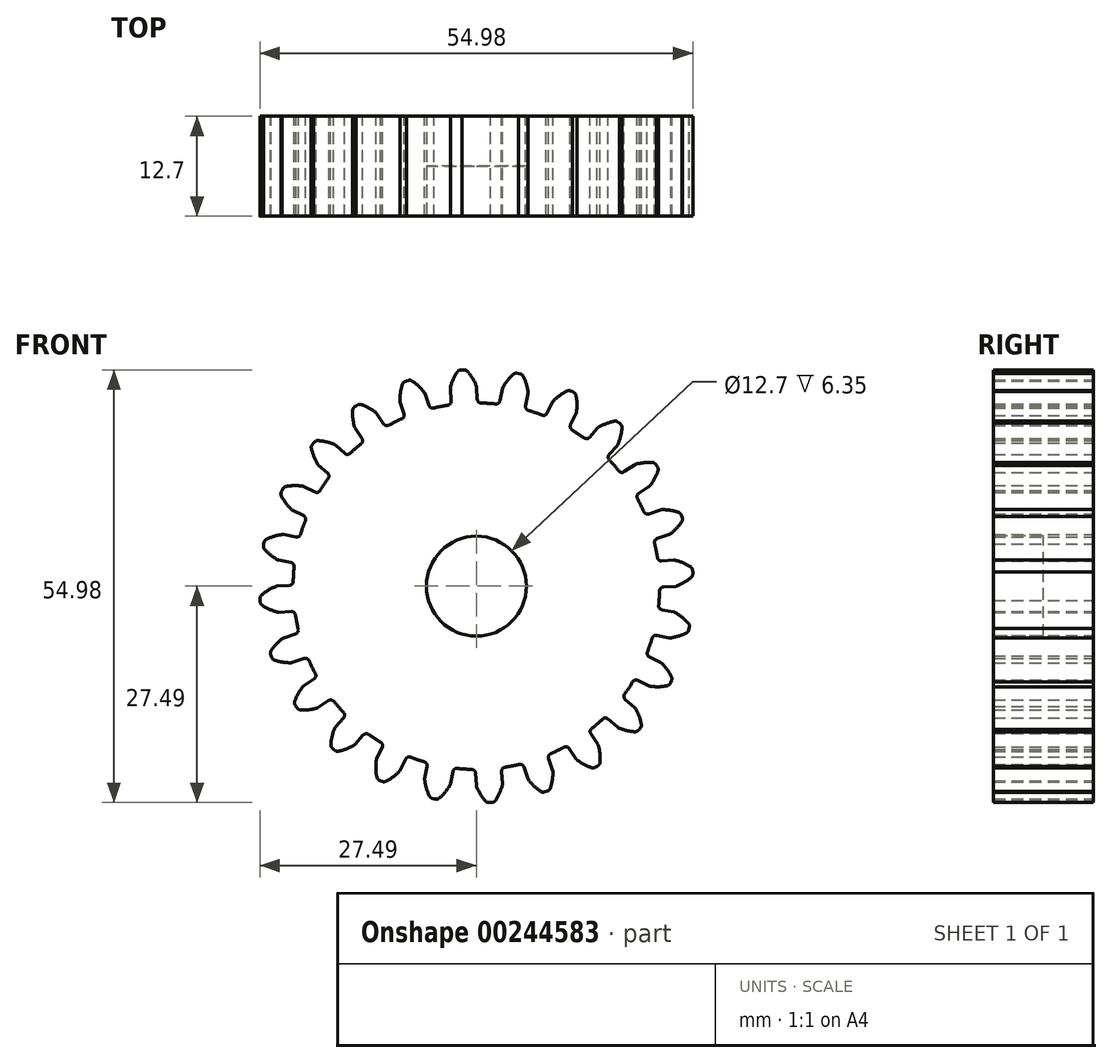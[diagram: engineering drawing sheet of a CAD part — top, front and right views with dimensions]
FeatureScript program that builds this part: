
annotation { "Feature Type Name" : "Feature", "Feature Type Description" : "" }
export const myFeature = defineFeature(function(context is Context, id is Id, definition is map)
    precondition{}
    {
        {
            var Q0;
            Q0=qCreatedBy(makeId("Front.planeOp"),FACE);
            var sketch = newSketch(context, id + "F0", { "sketchPlane" : qUnion([Q0])});
            skArc(sketch, "E0", {"start": v(-3.63, 23) * mm, "mid": v(-4.54, 22.83) * mm, "end": v(-5.44, 22.63) * mm});
            skArc(sketch, "E1", {"start": v(-0.03, 25.48) * mm, "mid": v(-0.52, 26.45) * mm, "end": v(-1.16, 27.32) * mm});
            skLineSegment(sketch, "E2", {"start": v(-1.54, 27.49) * mm, "end": v(-1.8, 27.49) * mm});
            skLineSegment(sketch, "E3", {"start": v(0, 25.32) * mm, "end": v(0.1, 23.75) * mm});
            skLineSegment(sketch, "E4.MirrorCS", {"start": v(-2.06, 27.46) * mm, "end": v(-1.8, 27.49) * mm});
            skArc(sketch, "E5.MirrorCS", {"start": v(-3.3, 25.26) * mm, "mid": v(-2.94, 26.29) * mm, "end": v(-2.41, 27.23) * mm});
            skLineSegment(sketch, "E6.MirrorCS", {"start": v(-3.31, 25.1) * mm, "end": v(-3.2, 23.53) * mm});
            skPoint(sketch, "E7.visualSharp", {"position": v(-3.18, 23.06) * mm});
            skArc(sketch, "E7.filletArc", {"start": v(-3.63, 23) * mm, "mid": v(-3.32, 23.18) * mm, "end": v(-3.2, 23.53) * mm});
            skPoint(sketch, "E8.visualSharp", {"position": v(0.14, 23.28) * mm});
            skArc(sketch, "E8.filletArc", {"start": v(0.1, 23.75) * mm, "mid": v(0.26, 23.41) * mm, "end": v(0.6, 23.27) * mm});
            skPoint(sketch, "E9.visualSharp", {"position": v(0, 25.4) * mm});
            skArc(sketch, "E9.filletArc", {"start": v(0, 25.32) * mm, "mid": v(0, 25.4) * mm, "end": v(-0.03, 25.48) * mm});
            skPoint(sketch, "E10.visualSharp", {"position": v(-1.32, 27.49) * mm});
            skArc(sketch, "E10.filletArc", {"start": v(-1.16, 27.32) * mm, "mid": v(-1.33, 27.44) * mm, "end": v(-1.54, 27.49) * mm});
            skPoint(sketch, "E11.visualSharp", {"position": v(-2.28, 27.43) * mm});
            skArc(sketch, "E11.filletArc", {"start": v(-2.06, 27.46) * mm, "mid": v(-2.26, 27.38) * mm, "end": v(-2.41, 27.23) * mm});
            skPoint(sketch, "E12.visualSharp", {"position": v(-3.32, 25.18) * mm});
            skArc(sketch, "E12.filletArc", {"start": v(-3.3, 25.26) * mm, "mid": v(-3.3, 25.18) * mm, "end": v(-3.31, 25.1) * mm});
            skArc(sketch, "E13.1.0", {"start": v(-9.46, 21.27) * mm, "mid": v(-9.2, 21.53) * mm, "end": v(-9.19, 21.9) * mm});
            skLineSegment(sketch, "E13.1.1", {"start": v(-9.7, 23.4) * mm, "end": v(-9.19, 21.9) * mm});
            skArc(sketch, "E13.1.2", {"start": v(-6.04, 22.96) * mm, "mid": v(-5.8, 22.68) * mm, "end": v(-5.44, 22.63) * mm});
            skLineSegment(sketch, "E13.1.3", {"start": v(-6.55, 24.46) * mm, "end": v(-6.04, 22.96) * mm});
            skArc(sketch, "E13.1.4", {"start": v(-6.62, 24.6) * mm, "mid": v(-7.34, 25.41) * mm, "end": v(-8.2, 26.09) * mm});
            skArc(sketch, "E13.1.5", {"start": v(-9.72, 23.55) * mm, "mid": v(-9.64, 24.63) * mm, "end": v(-9.38, 25.68) * mm});
            skArc(sketch, "E13.1.6", {"start": v(-9.1, 25.99) * mm, "mid": v(-9.27, 25.87) * mm, "end": v(-9.38, 25.68) * mm});
            skLineSegment(sketch, "E13.1.7", {"start": v(-8.6, 26.15) * mm, "end": v(-8.86, 26.09) * mm});
            skLineSegment(sketch, "E13.1.8", {"start": v(-9.1, 25.99) * mm, "end": v(-8.86, 26.09) * mm});
            skArc(sketch, "E13.1.9", {"start": v(-8.2, 26.09) * mm, "mid": v(-8.4, 26.16) * mm, "end": v(-8.6, 26.15) * mm});
            skArc(sketch, "E13.1.10", {"start": v(-6.55, 24.46) * mm, "mid": v(-6.58, 24.53) * mm, "end": v(-6.62, 24.6) * mm});
            skArc(sketch, "E13.1.11", {"start": v(-9.72, 23.55) * mm, "mid": v(-9.71, 23.47) * mm, "end": v(-9.7, 23.4) * mm});
            skArc(sketch, "E13.2.0", {"start": v(-14.64, 18.1) * mm, "mid": v(-14.46, 18.41) * mm, "end": v(-14.54, 18.77) * mm});
            skLineSegment(sketch, "E13.2.1", {"start": v(-15.42, 20.09) * mm, "end": v(-14.54, 18.77) * mm});
            skArc(sketch, "E13.2.2", {"start": v(-11.78, 20.62) * mm, "mid": v(-11.48, 20.4) * mm, "end": v(-11.11, 20.45) * mm});
            skLineSegment(sketch, "E13.2.3", {"start": v(-12.66, 21.93) * mm, "end": v(-11.78, 20.62) * mm});
            skArc(sketch, "E13.2.4", {"start": v(-12.76, 22.05) * mm, "mid": v(-13.67, 22.64) * mm, "end": v(-14.66, 23.08) * mm});
            skArc(sketch, "E13.2.5", {"start": v(-15.49, 20.23) * mm, "mid": v(-15.69, 21.3) * mm, "end": v(-15.7, 22.38) * mm});
            skArc(sketch, "E13.2.6", {"start": v(-15.51, 22.75) * mm, "mid": v(-15.65, 22.58) * mm, "end": v(-15.7, 22.38) * mm});
            skLineSegment(sketch, "E13.2.7", {"start": v(-15.08, 23.04) * mm, "end": v(-15.3, 22.9) * mm});
            skLineSegment(sketch, "E13.2.8", {"start": v(-15.51, 22.75) * mm, "end": v(-15.3, 22.9) * mm});
            skArc(sketch, "E13.2.9", {"start": v(-14.66, 23.08) * mm, "mid": v(-14.88, 23.1) * mm, "end": v(-15.08, 23.04) * mm});
            skArc(sketch, "E13.2.10", {"start": v(-12.66, 21.93) * mm, "mid": v(-12.7, 22) * mm, "end": v(-12.76, 22.05) * mm});
            skArc(sketch, "E13.2.11", {"start": v(-15.49, 20.23) * mm, "mid": v(-15.46, 20.16) * mm, "end": v(-15.42, 20.09) * mm});
            skArc(sketch, "E13.3.0", {"start": v(-18.83, 13.69) * mm, "mid": v(-18.73, 14.04) * mm, "end": v(-18.9, 14.37) * mm});
            skLineSegment(sketch, "E13.3.1", {"start": v(-20.1, 15.41) * mm, "end": v(-18.9, 14.37) * mm});
            skArc(sketch, "E13.3.2", {"start": v(-16.71, 16.87) * mm, "mid": v(-16.37, 16.74) * mm, "end": v(-16.03, 16.88) * mm});
            skLineSegment(sketch, "E13.3.3", {"start": v(-17.9, 17.9) * mm, "end": v(-16.71, 16.87) * mm});
            skArc(sketch, "E13.3.4", {"start": v(-18.04, 18) * mm, "mid": v(-19.06, 18.33) * mm, "end": v(-20.14, 18.5) * mm});
            skArc(sketch, "E13.3.5", {"start": v(-20.2, 15.53) * mm, "mid": v(-20.67, 16.5) * mm, "end": v(-20.97, 17.55) * mm});
            skArc(sketch, "E13.3.6", {"start": v(-20.87, 17.96) * mm, "mid": v(-20.96, 17.76) * mm, "end": v(-20.97, 17.55) * mm});
            skLineSegment(sketch, "E13.3.7", {"start": v(-20.53, 18.35) * mm, "end": v(-20.71, 18.16) * mm});
            skLineSegment(sketch, "E13.3.8", {"start": v(-20.87, 17.96) * mm, "end": v(-20.71, 18.16) * mm});
            skArc(sketch, "E13.3.9", {"start": v(-20.14, 18.5) * mm, "mid": v(-20.35, 18.46) * mm, "end": v(-20.53, 18.35) * mm});
            skArc(sketch, "E13.3.10", {"start": v(-17.9, 17.9) * mm, "mid": v(-17.97, 17.96) * mm, "end": v(-18.04, 18) * mm});
            skArc(sketch, "E13.3.11", {"start": v(-20.2, 15.53) * mm, "mid": v(-20.15, 15.47) * mm, "end": v(-20.1, 15.41) * mm});
            skArc(sketch, "E13.4.0", {"start": v(-21.73, 8.35) * mm, "mid": v(-21.73, 8.72) * mm, "end": v(-21.98, 8.99) * mm});
            skLineSegment(sketch, "E13.4.1", {"start": v(-23.4, 9.69) * mm, "end": v(-21.98, 8.99) * mm});
            skArc(sketch, "E13.4.2", {"start": v(-20.51, 11.97) * mm, "mid": v(-20.14, 11.93) * mm, "end": v(-19.85, 12.16) * mm});
            skLineSegment(sketch, "E13.4.3", {"start": v(-21.93, 12.67) * mm, "end": v(-20.51, 11.97) * mm});
            skArc(sketch, "E13.4.4", {"start": v(-22.08, 12.71) * mm, "mid": v(-23.16, 12.78) * mm, "end": v(-24.24, 12.65) * mm});
            skArc(sketch, "E13.4.5", {"start": v(-23.53, 9.78) * mm, "mid": v(-24.23, 10.6) * mm, "end": v(-24.8, 11.53) * mm});
            skArc(sketch, "E13.4.6", {"start": v(-24.8, 11.94) * mm, "mid": v(-24.85, 11.73) * mm, "end": v(-24.8, 11.53) * mm});
            skLineSegment(sketch, "E13.4.7", {"start": v(-24.58, 12.4) * mm, "end": v(-24.7, 12.18) * mm});
            skLineSegment(sketch, "E13.4.8", {"start": v(-24.8, 11.94) * mm, "end": v(-24.7, 12.18) * mm});
            skArc(sketch, "E13.4.9", {"start": v(-24.24, 12.65) * mm, "mid": v(-24.43, 12.57) * mm, "end": v(-24.58, 12.4) * mm});
            skArc(sketch, "E13.4.10", {"start": v(-21.93, 12.67) * mm, "mid": v(-22, 12.7) * mm, "end": v(-22.08, 12.71) * mm});
            skArc(sketch, "E13.4.11", {"start": v(-23.53, 9.78) * mm, "mid": v(-23.46, 9.73) * mm, "end": v(-23.4, 9.69) * mm});
            skArc(sketch, "E13.5.0", {"start": v(-23.15, 2.44) * mm, "mid": v(-23.25, 2.8) * mm, "end": v(-23.56, 3) * mm});
            skLineSegment(sketch, "E13.5.1", {"start": v(-25.1, 3.3) * mm, "end": v(-23.56, 3) * mm});
            skArc(sketch, "E13.5.2", {"start": v(-22.9, 6.25) * mm, "mid": v(-22.55, 6.31) * mm, "end": v(-22.32, 6.6) * mm});
            skLineSegment(sketch, "E13.5.3", {"start": v(-24.46, 6.56) * mm, "end": v(-22.9, 6.25) * mm});
            skArc(sketch, "E13.5.4", {"start": v(-24.62, 6.56) * mm, "mid": v(-25.68, 6.35) * mm, "end": v(-26.69, 5.95) * mm});
            skArc(sketch, "E13.5.5", {"start": v(-25.25, 3.36) * mm, "mid": v(-26.15, 3.96) * mm, "end": v(-26.93, 4.72) * mm});
            skArc(sketch, "E13.5.6", {"start": v(-27.05, 5.12) * mm, "mid": v(-27.04, 4.9) * mm, "end": v(-26.93, 4.72) * mm});
            skLineSegment(sketch, "E13.5.7", {"start": v(-26.95, 5.63) * mm, "end": v(-27.02, 5.37) * mm});
            skLineSegment(sketch, "E13.5.8", {"start": v(-27.05, 5.12) * mm, "end": v(-27.02, 5.37) * mm});
            skArc(sketch, "E13.5.9", {"start": v(-26.69, 5.95) * mm, "mid": v(-26.85, 5.82) * mm, "end": v(-26.95, 5.63) * mm});
            skArc(sketch, "E13.5.10", {"start": v(-24.46, 6.56) * mm, "mid": v(-24.54, 6.57) * mm, "end": v(-24.62, 6.56) * mm});
            skArc(sketch, "E13.5.11", {"start": v(-25.25, 3.36) * mm, "mid": v(-25.18, 3.32) * mm, "end": v(-25.1, 3.3) * mm});
            skArc(sketch, "E13.6.0", {"start": v(-23, -3.63) * mm, "mid": v(-23.18, -3.32) * mm, "end": v(-23.53, -3.2) * mm});
            skLineSegment(sketch, "E13.6.1", {"start": v(-25.1, -3.31) * mm, "end": v(-23.53, -3.2) * mm});
            skArc(sketch, "E13.6.2", {"start": v(-23.75, 0.1) * mm, "mid": v(-23.41, 0.26) * mm, "end": v(-23.27, 0.6) * mm});
            skLineSegment(sketch, "E13.6.3", {"start": v(-25.32, 0) * mm, "end": v(-23.75, 0.1) * mm});
            skArc(sketch, "E13.6.4", {"start": v(-25.48, -0.03) * mm, "mid": v(-26.45, -0.52) * mm, "end": v(-27.32, -1.16) * mm});
            skArc(sketch, "E13.6.5", {"start": v(-25.26, -3.3) * mm, "mid": v(-26.29, -2.94) * mm, "end": v(-27.23, -2.41) * mm});
            skArc(sketch, "E13.6.6", {"start": v(-27.46, -2.06) * mm, "mid": v(-27.38, -2.26) * mm, "end": v(-27.23, -2.41) * mm});
            skLineSegment(sketch, "E13.6.7", {"start": v(-27.49, -1.54) * mm, "end": v(-27.49, -1.8) * mm});
            skLineSegment(sketch, "E13.6.8", {"start": v(-27.46, -2.06) * mm, "end": v(-27.49, -1.8) * mm});
            skArc(sketch, "E13.6.9", {"start": v(-27.32, -1.16) * mm, "mid": v(-27.44, -1.33) * mm, "end": v(-27.49, -1.54) * mm});
            skArc(sketch, "E13.6.10", {"start": v(-25.32, 0) * mm, "mid": v(-25.4, 0) * mm, "end": v(-25.48, -0.03) * mm});
            skArc(sketch, "E13.6.11", {"start": v(-25.26, -3.3) * mm, "mid": v(-25.18, -3.3) * mm, "end": v(-25.1, -3.31) * mm});
            skArc(sketch, "E13.7.0", {"start": v(-21.27, -9.46) * mm, "mid": v(-21.53, -9.2) * mm, "end": v(-21.9, -9.19) * mm});
            skLineSegment(sketch, "E13.7.1", {"start": v(-23.4, -9.7) * mm, "end": v(-21.9, -9.19) * mm});
            skArc(sketch, "E13.7.2", {"start": v(-22.96, -6.04) * mm, "mid": v(-22.68, -5.8) * mm, "end": v(-22.63, -5.44) * mm});
            skLineSegment(sketch, "E13.7.3", {"start": v(-24.46, -6.55) * mm, "end": v(-22.96, -6.04) * mm});
            skArc(sketch, "E13.7.4", {"start": v(-24.6, -6.62) * mm, "mid": v(-25.41, -7.34) * mm, "end": v(-26.09, -8.2) * mm});
            skArc(sketch, "E13.7.5", {"start": v(-23.55, -9.72) * mm, "mid": v(-24.63, -9.64) * mm, "end": v(-25.68, -9.38) * mm});
            skArc(sketch, "E13.7.6", {"start": v(-25.99, -9.1) * mm, "mid": v(-25.87, -9.27) * mm, "end": v(-25.68, -9.38) * mm});
            skLineSegment(sketch, "E13.7.7", {"start": v(-26.15, -8.6) * mm, "end": v(-26.09, -8.86) * mm});
            skLineSegment(sketch, "E13.7.8", {"start": v(-25.99, -9.1) * mm, "end": v(-26.09, -8.86) * mm});
            skArc(sketch, "E13.7.9", {"start": v(-26.09, -8.2) * mm, "mid": v(-26.16, -8.4) * mm, "end": v(-26.15, -8.6) * mm});
            skArc(sketch, "E13.7.10", {"start": v(-24.46, -6.55) * mm, "mid": v(-24.53, -6.58) * mm, "end": v(-24.6, -6.62) * mm});
            skArc(sketch, "E13.7.11", {"start": v(-23.55, -9.72) * mm, "mid": v(-23.47, -9.71) * mm, "end": v(-23.4, -9.7) * mm});
            skArc(sketch, "E13.8.0", {"start": v(-18.1, -14.64) * mm, "mid": v(-18.41, -14.46) * mm, "end": v(-18.77, -14.54) * mm});
            skLineSegment(sketch, "E13.8.1", {"start": v(-20.09, -15.42) * mm, "end": v(-18.77, -14.54) * mm});
            skArc(sketch, "E13.8.2", {"start": v(-20.62, -11.78) * mm, "mid": v(-20.4, -11.48) * mm, "end": v(-20.45, -11.11) * mm});
            skLineSegment(sketch, "E13.8.3", {"start": v(-21.93, -12.66) * mm, "end": v(-20.62, -11.78) * mm});
            skArc(sketch, "E13.8.4", {"start": v(-22.05, -12.76) * mm, "mid": v(-22.64, -13.67) * mm, "end": v(-23.08, -14.66) * mm});
            skArc(sketch, "E13.8.5", {"start": v(-20.23, -15.49) * mm, "mid": v(-21.3, -15.69) * mm, "end": v(-22.38, -15.7) * mm});
            skArc(sketch, "E13.8.6", {"start": v(-22.75, -15.51) * mm, "mid": v(-22.58, -15.65) * mm, "end": v(-22.38, -15.7) * mm});
            skLineSegment(sketch, "E13.8.7", {"start": v(-23.04, -15.08) * mm, "end": v(-22.9, -15.3) * mm});
            skLineSegment(sketch, "E13.8.8", {"start": v(-22.75, -15.51) * mm, "end": v(-22.9, -15.3) * mm});
            skArc(sketch, "E13.8.9", {"start": v(-23.08, -14.66) * mm, "mid": v(-23.1, -14.88) * mm, "end": v(-23.04, -15.08) * mm});
            skArc(sketch, "E13.8.10", {"start": v(-21.93, -12.66) * mm, "mid": v(-22, -12.7) * mm, "end": v(-22.05, -12.76) * mm});
            skArc(sketch, "E13.8.11", {"start": v(-20.23, -15.49) * mm, "mid": v(-20.16, -15.46) * mm, "end": v(-20.09, -15.42) * mm});
            skArc(sketch, "E13.9.0", {"start": v(-13.69, -18.83) * mm, "mid": v(-14.04, -18.73) * mm, "end": v(-14.37, -18.9) * mm});
            skLineSegment(sketch, "E13.9.1", {"start": v(-15.41, -20.1) * mm, "end": v(-14.37, -18.9) * mm});
            skArc(sketch, "E13.9.2", {"start": v(-16.87, -16.71) * mm, "mid": v(-16.74, -16.37) * mm, "end": v(-16.88, -16.03) * mm});
            skLineSegment(sketch, "E13.9.3", {"start": v(-17.9, -17.9) * mm, "end": v(-16.87, -16.71) * mm});
            skArc(sketch, "E13.9.4", {"start": v(-18, -18.04) * mm, "mid": v(-18.33, -19.06) * mm, "end": v(-18.5, -20.14) * mm});
            skArc(sketch, "E13.9.5", {"start": v(-15.53, -20.2) * mm, "mid": v(-16.5, -20.67) * mm, "end": v(-17.55, -20.97) * mm});
            skArc(sketch, "E13.9.6", {"start": v(-17.96, -20.87) * mm, "mid": v(-17.76, -20.96) * mm, "end": v(-17.55, -20.97) * mm});
            skLineSegment(sketch, "E13.9.7", {"start": v(-18.35, -20.53) * mm, "end": v(-18.16, -20.71) * mm});
            skLineSegment(sketch, "E13.9.8", {"start": v(-17.96, -20.87) * mm, "end": v(-18.16, -20.71) * mm});
            skArc(sketch, "E13.9.9", {"start": v(-18.5, -20.14) * mm, "mid": v(-18.46, -20.35) * mm, "end": v(-18.35, -20.53) * mm});
            skArc(sketch, "E13.9.10", {"start": v(-17.9, -17.9) * mm, "mid": v(-17.96, -17.97) * mm, "end": v(-18, -18.04) * mm});
            skArc(sketch, "E13.9.11", {"start": v(-15.53, -20.2) * mm, "mid": v(-15.47, -20.15) * mm, "end": v(-15.41, -20.1) * mm});
            skArc(sketch, "E13.10.0", {"start": v(-8.35, -21.73) * mm, "mid": v(-8.72, -21.73) * mm, "end": v(-8.99, -21.98) * mm});
            skLineSegment(sketch, "E13.10.1", {"start": v(-9.69, -23.4) * mm, "end": v(-8.99, -21.98) * mm});
            skArc(sketch, "E13.10.2", {"start": v(-11.97, -20.51) * mm, "mid": v(-11.93, -20.14) * mm, "end": v(-12.16, -19.85) * mm});
            skLineSegment(sketch, "E13.10.3", {"start": v(-12.67, -21.93) * mm, "end": v(-11.97, -20.51) * mm});
            skArc(sketch, "E13.10.4", {"start": v(-12.71, -22.08) * mm, "mid": v(-12.78, -23.16) * mm, "end": v(-12.65, -24.24) * mm});
            skArc(sketch, "E13.10.5", {"start": v(-9.78, -23.53) * mm, "mid": v(-10.6, -24.23) * mm, "end": v(-11.53, -24.8) * mm});
            skArc(sketch, "E13.10.6", {"start": v(-11.94, -24.8) * mm, "mid": v(-11.73, -24.85) * mm, "end": v(-11.53, -24.8) * mm});
            skLineSegment(sketch, "E13.10.7", {"start": v(-12.4, -24.58) * mm, "end": v(-12.18, -24.7) * mm});
            skLineSegment(sketch, "E13.10.8", {"start": v(-11.94, -24.8) * mm, "end": v(-12.18, -24.7) * mm});
            skArc(sketch, "E13.10.9", {"start": v(-12.65, -24.24) * mm, "mid": v(-12.57, -24.43) * mm, "end": v(-12.4, -24.58) * mm});
            skArc(sketch, "E13.10.10", {"start": v(-12.67, -21.93) * mm, "mid": v(-12.7, -22) * mm, "end": v(-12.71, -22.08) * mm});
            skArc(sketch, "E13.10.11", {"start": v(-9.78, -23.53) * mm, "mid": v(-9.73, -23.46) * mm, "end": v(-9.69, -23.4) * mm});
            skArc(sketch, "E13.11.0", {"start": v(-2.44, -23.15) * mm, "mid": v(-2.8, -23.25) * mm, "end": v(-3, -23.56) * mm});
            skLineSegment(sketch, "E13.11.1", {"start": v(-3.3, -25.1) * mm, "end": v(-3, -23.56) * mm});
            skArc(sketch, "E13.11.2", {"start": v(-6.25, -22.9) * mm, "mid": v(-6.31, -22.55) * mm, "end": v(-6.6, -22.32) * mm});
            skLineSegment(sketch, "E13.11.3", {"start": v(-6.56, -24.46) * mm, "end": v(-6.25, -22.9) * mm});
            skArc(sketch, "E13.11.4", {"start": v(-6.56, -24.62) * mm, "mid": v(-6.35, -25.68) * mm, "end": v(-5.95, -26.69) * mm});
            skArc(sketch, "E13.11.5", {"start": v(-3.36, -25.25) * mm, "mid": v(-3.96, -26.15) * mm, "end": v(-4.72, -26.93) * mm});
            skArc(sketch, "E13.11.6", {"start": v(-5.12, -27.05) * mm, "mid": v(-4.9, -27.04) * mm, "end": v(-4.72, -26.93) * mm});
            skLineSegment(sketch, "E13.11.7", {"start": v(-5.63, -26.95) * mm, "end": v(-5.37, -27.02) * mm});
            skLineSegment(sketch, "E13.11.8", {"start": v(-5.12, -27.05) * mm, "end": v(-5.37, -27.02) * mm});
            skArc(sketch, "E13.11.9", {"start": v(-5.95, -26.69) * mm, "mid": v(-5.82, -26.85) * mm, "end": v(-5.63, -26.95) * mm});
            skArc(sketch, "E13.11.10", {"start": v(-6.56, -24.46) * mm, "mid": v(-6.57, -24.54) * mm, "end": v(-6.56, -24.62) * mm});
            skArc(sketch, "E13.11.11", {"start": v(-3.36, -25.25) * mm, "mid": v(-3.32, -25.18) * mm, "end": v(-3.3, -25.1) * mm});
            skArc(sketch, "E13.12.0", {"start": v(3.63, -23) * mm, "mid": v(3.32, -23.18) * mm, "end": v(3.2, -23.53) * mm});
            skLineSegment(sketch, "E13.12.1", {"start": v(3.31, -25.1) * mm, "end": v(3.2, -23.53) * mm});
            skArc(sketch, "E13.12.2", {"start": v(-0.1, -23.75) * mm, "mid": v(-0.26, -23.41) * mm, "end": v(-0.6, -23.27) * mm});
            skLineSegment(sketch, "E13.12.3", {"start": v(0, -25.32) * mm, "end": v(-0.1, -23.75) * mm});
            skArc(sketch, "E13.12.4", {"start": v(0.03, -25.48) * mm, "mid": v(0.52, -26.45) * mm, "end": v(1.16, -27.32) * mm});
            skArc(sketch, "E13.12.5", {"start": v(3.3, -25.26) * mm, "mid": v(2.94, -26.29) * mm, "end": v(2.41, -27.23) * mm});
            skArc(sketch, "E13.12.6", {"start": v(2.06, -27.46) * mm, "mid": v(2.26, -27.38) * mm, "end": v(2.41, -27.23) * mm});
            skLineSegment(sketch, "E13.12.7", {"start": v(1.54, -27.49) * mm, "end": v(1.8, -27.49) * mm});
            skLineSegment(sketch, "E13.12.8", {"start": v(2.06, -27.46) * mm, "end": v(1.8, -27.49) * mm});
            skArc(sketch, "E13.12.9", {"start": v(1.16, -27.32) * mm, "mid": v(1.33, -27.44) * mm, "end": v(1.54, -27.49) * mm});
            skArc(sketch, "E13.12.10", {"start": v(0, -25.32) * mm, "mid": v(0, -25.4) * mm, "end": v(0.03, -25.48) * mm});
            skArc(sketch, "E13.12.11", {"start": v(3.3, -25.26) * mm, "mid": v(3.3, -25.18) * mm, "end": v(3.31, -25.1) * mm});
            skArc(sketch, "E13.13.0", {"start": v(9.46, -21.27) * mm, "mid": v(9.2, -21.53) * mm, "end": v(9.19, -21.9) * mm});
            skLineSegment(sketch, "E13.13.1", {"start": v(9.7, -23.4) * mm, "end": v(9.19, -21.9) * mm});
            skArc(sketch, "E13.13.2", {"start": v(6.04, -22.96) * mm, "mid": v(5.8, -22.68) * mm, "end": v(5.44, -22.63) * mm});
            skLineSegment(sketch, "E13.13.3", {"start": v(6.55, -24.46) * mm, "end": v(6.04, -22.96) * mm});
            skArc(sketch, "E13.13.4", {"start": v(6.62, -24.6) * mm, "mid": v(7.34, -25.41) * mm, "end": v(8.2, -26.09) * mm});
            skArc(sketch, "E13.13.5", {"start": v(9.72, -23.55) * mm, "mid": v(9.64, -24.63) * mm, "end": v(9.38, -25.68) * mm});
            skArc(sketch, "E13.13.6", {"start": v(9.1, -25.99) * mm, "mid": v(9.27, -25.87) * mm, "end": v(9.38, -25.68) * mm});
            skLineSegment(sketch, "E13.13.7", {"start": v(8.6, -26.15) * mm, "end": v(8.86, -26.09) * mm});
            skLineSegment(sketch, "E13.13.8", {"start": v(9.1, -25.99) * mm, "end": v(8.86, -26.09) * mm});
            skArc(sketch, "E13.13.9", {"start": v(8.2, -26.09) * mm, "mid": v(8.4, -26.16) * mm, "end": v(8.6, -26.15) * mm});
            skArc(sketch, "E13.13.10", {"start": v(6.55, -24.46) * mm, "mid": v(6.58, -24.53) * mm, "end": v(6.62, -24.6) * mm});
            skArc(sketch, "E13.13.11", {"start": v(9.72, -23.55) * mm, "mid": v(9.71, -23.47) * mm, "end": v(9.7, -23.4) * mm});
            skArc(sketch, "E13.14.0", {"start": v(14.64, -18.1) * mm, "mid": v(14.46, -18.41) * mm, "end": v(14.54, -18.77) * mm});
            skLineSegment(sketch, "E13.14.1", {"start": v(15.42, -20.09) * mm, "end": v(14.54, -18.77) * mm});
            skArc(sketch, "E13.14.2", {"start": v(11.78, -20.62) * mm, "mid": v(11.48, -20.4) * mm, "end": v(11.11, -20.45) * mm});
            skLineSegment(sketch, "E13.14.3", {"start": v(12.66, -21.93) * mm, "end": v(11.78, -20.62) * mm});
            skArc(sketch, "E13.14.4", {"start": v(12.76, -22.05) * mm, "mid": v(13.67, -22.64) * mm, "end": v(14.66, -23.08) * mm});
            skArc(sketch, "E13.14.5", {"start": v(15.49, -20.23) * mm, "mid": v(15.69, -21.3) * mm, "end": v(15.7, -22.38) * mm});
            skArc(sketch, "E13.14.6", {"start": v(15.51, -22.75) * mm, "mid": v(15.65, -22.58) * mm, "end": v(15.7, -22.38) * mm});
            skLineSegment(sketch, "E13.14.7", {"start": v(15.08, -23.04) * mm, "end": v(15.3, -22.9) * mm});
            skLineSegment(sketch, "E13.14.8", {"start": v(15.51, -22.75) * mm, "end": v(15.3, -22.9) * mm});
            skArc(sketch, "E13.14.9", {"start": v(14.66, -23.08) * mm, "mid": v(14.88, -23.1) * mm, "end": v(15.08, -23.04) * mm});
            skArc(sketch, "E13.14.10", {"start": v(12.66, -21.93) * mm, "mid": v(12.7, -22) * mm, "end": v(12.76, -22.05) * mm});
            skArc(sketch, "E13.14.11", {"start": v(15.49, -20.23) * mm, "mid": v(15.46, -20.16) * mm, "end": v(15.42, -20.09) * mm});
            skArc(sketch, "E13.15.0", {"start": v(18.83, -13.69) * mm, "mid": v(18.73, -14.04) * mm, "end": v(18.9, -14.37) * mm});
            skLineSegment(sketch, "E13.15.1", {"start": v(20.1, -15.41) * mm, "end": v(18.9, -14.37) * mm});
            skArc(sketch, "E13.15.2", {"start": v(16.71, -16.87) * mm, "mid": v(16.37, -16.74) * mm, "end": v(16.03, -16.88) * mm});
            skLineSegment(sketch, "E13.15.3", {"start": v(17.9, -17.9) * mm, "end": v(16.71, -16.87) * mm});
            skArc(sketch, "E13.15.4", {"start": v(18.04, -18) * mm, "mid": v(19.06, -18.33) * mm, "end": v(20.14, -18.5) * mm});
            skArc(sketch, "E13.15.5", {"start": v(20.2, -15.53) * mm, "mid": v(20.67, -16.5) * mm, "end": v(20.97, -17.55) * mm});
            skArc(sketch, "E13.15.6", {"start": v(20.87, -17.96) * mm, "mid": v(20.96, -17.76) * mm, "end": v(20.97, -17.55) * mm});
            skLineSegment(sketch, "E13.15.7", {"start": v(20.53, -18.35) * mm, "end": v(20.71, -18.16) * mm});
            skLineSegment(sketch, "E13.15.8", {"start": v(20.87, -17.96) * mm, "end": v(20.71, -18.16) * mm});
            skArc(sketch, "E13.15.9", {"start": v(20.14, -18.5) * mm, "mid": v(20.35, -18.46) * mm, "end": v(20.53, -18.35) * mm});
            skArc(sketch, "E13.15.10", {"start": v(17.9, -17.9) * mm, "mid": v(17.97, -17.96) * mm, "end": v(18.04, -18) * mm});
            skArc(sketch, "E13.15.11", {"start": v(20.2, -15.53) * mm, "mid": v(20.15, -15.47) * mm, "end": v(20.1, -15.41) * mm});
            skArc(sketch, "E13.16.0", {"start": v(21.73, -8.35) * mm, "mid": v(21.73, -8.72) * mm, "end": v(21.98, -8.99) * mm});
            skLineSegment(sketch, "E13.16.1", {"start": v(23.4, -9.69) * mm, "end": v(21.98, -8.99) * mm});
            skArc(sketch, "E13.16.2", {"start": v(20.51, -11.97) * mm, "mid": v(20.14, -11.93) * mm, "end": v(19.85, -12.16) * mm});
            skLineSegment(sketch, "E13.16.3", {"start": v(21.93, -12.67) * mm, "end": v(20.51, -11.97) * mm});
            skArc(sketch, "E13.16.4", {"start": v(22.08, -12.71) * mm, "mid": v(23.16, -12.78) * mm, "end": v(24.24, -12.65) * mm});
            skArc(sketch, "E13.16.5", {"start": v(23.53, -9.78) * mm, "mid": v(24.23, -10.6) * mm, "end": v(24.8, -11.53) * mm});
            skArc(sketch, "E13.16.6", {"start": v(24.8, -11.94) * mm, "mid": v(24.85, -11.73) * mm, "end": v(24.8, -11.53) * mm});
            skLineSegment(sketch, "E13.16.7", {"start": v(24.58, -12.4) * mm, "end": v(24.7, -12.18) * mm});
            skLineSegment(sketch, "E13.16.8", {"start": v(24.8, -11.94) * mm, "end": v(24.7, -12.18) * mm});
            skArc(sketch, "E13.16.9", {"start": v(24.24, -12.65) * mm, "mid": v(24.43, -12.57) * mm, "end": v(24.58, -12.4) * mm});
            skArc(sketch, "E13.16.10", {"start": v(21.93, -12.67) * mm, "mid": v(22, -12.7) * mm, "end": v(22.08, -12.71) * mm});
            skArc(sketch, "E13.16.11", {"start": v(23.53, -9.78) * mm, "mid": v(23.46, -9.73) * mm, "end": v(23.4, -9.69) * mm});
            skArc(sketch, "E13.17.0", {"start": v(23.15, -2.44) * mm, "mid": v(23.25, -2.8) * mm, "end": v(23.56, -3) * mm});
            skLineSegment(sketch, "E13.17.1", {"start": v(25.1, -3.3) * mm, "end": v(23.56, -3) * mm});
            skArc(sketch, "E13.17.2", {"start": v(22.9, -6.25) * mm, "mid": v(22.55, -6.31) * mm, "end": v(22.32, -6.6) * mm});
            skLineSegment(sketch, "E13.17.3", {"start": v(24.46, -6.56) * mm, "end": v(22.9, -6.25) * mm});
            skArc(sketch, "E13.17.4", {"start": v(24.62, -6.56) * mm, "mid": v(25.68, -6.35) * mm, "end": v(26.69, -5.95) * mm});
            skArc(sketch, "E13.17.5", {"start": v(25.25, -3.36) * mm, "mid": v(26.15, -3.96) * mm, "end": v(26.93, -4.72) * mm});
            skArc(sketch, "E13.17.6", {"start": v(27.05, -5.12) * mm, "mid": v(27.04, -4.9) * mm, "end": v(26.93, -4.72) * mm});
            skLineSegment(sketch, "E13.17.7", {"start": v(26.95, -5.63) * mm, "end": v(27.02, -5.37) * mm});
            skLineSegment(sketch, "E13.17.8", {"start": v(27.05, -5.12) * mm, "end": v(27.02, -5.37) * mm});
            skArc(sketch, "E13.17.9", {"start": v(26.69, -5.95) * mm, "mid": v(26.85, -5.82) * mm, "end": v(26.95, -5.63) * mm});
            skArc(sketch, "E13.17.10", {"start": v(24.46, -6.56) * mm, "mid": v(24.54, -6.57) * mm, "end": v(24.62, -6.56) * mm});
            skArc(sketch, "E13.17.11", {"start": v(25.25, -3.36) * mm, "mid": v(25.18, -3.32) * mm, "end": v(25.1, -3.3) * mm});
            skArc(sketch, "E13.18.0", {"start": v(23, 3.63) * mm, "mid": v(23.18, 3.32) * mm, "end": v(23.53, 3.2) * mm});
            skLineSegment(sketch, "E13.18.1", {"start": v(25.1, 3.31) * mm, "end": v(23.53, 3.2) * mm});
            skArc(sketch, "E13.18.2", {"start": v(23.75, -0.1) * mm, "mid": v(23.41, -0.26) * mm, "end": v(23.27, -0.6) * mm});
            skLineSegment(sketch, "E13.18.3", {"start": v(25.32, 0) * mm, "end": v(23.75, -0.1) * mm});
            skArc(sketch, "E13.18.4", {"start": v(25.48, 0.03) * mm, "mid": v(26.45, 0.52) * mm, "end": v(27.32, 1.16) * mm});
            skArc(sketch, "E13.18.5", {"start": v(25.26, 3.3) * mm, "mid": v(26.29, 2.94) * mm, "end": v(27.23, 2.41) * mm});
            skArc(sketch, "E13.18.6", {"start": v(27.46, 2.06) * mm, "mid": v(27.38, 2.26) * mm, "end": v(27.23, 2.41) * mm});
            skLineSegment(sketch, "E13.18.7", {"start": v(27.49, 1.54) * mm, "end": v(27.49, 1.8) * mm});
            skLineSegment(sketch, "E13.18.8", {"start": v(27.46, 2.06) * mm, "end": v(27.49, 1.8) * mm});
            skArc(sketch, "E13.18.9", {"start": v(27.32, 1.16) * mm, "mid": v(27.44, 1.33) * mm, "end": v(27.49, 1.54) * mm});
            skArc(sketch, "E13.18.10", {"start": v(25.32, 0) * mm, "mid": v(25.4, 0) * mm, "end": v(25.48, 0.03) * mm});
            skArc(sketch, "E13.18.11", {"start": v(25.26, 3.3) * mm, "mid": v(25.18, 3.3) * mm, "end": v(25.1, 3.31) * mm});
            skArc(sketch, "E13.19.0", {"start": v(21.27, 9.46) * mm, "mid": v(21.53, 9.2) * mm, "end": v(21.9, 9.19) * mm});
            skLineSegment(sketch, "E13.19.1", {"start": v(23.4, 9.7) * mm, "end": v(21.9, 9.19) * mm});
            skArc(sketch, "E13.19.2", {"start": v(22.96, 6.04) * mm, "mid": v(22.68, 5.8) * mm, "end": v(22.63, 5.44) * mm});
            skLineSegment(sketch, "E13.19.3", {"start": v(24.46, 6.55) * mm, "end": v(22.96, 6.04) * mm});
            skArc(sketch, "E13.19.4", {"start": v(24.6, 6.62) * mm, "mid": v(25.41, 7.34) * mm, "end": v(26.09, 8.2) * mm});
            skArc(sketch, "E13.19.5", {"start": v(23.55, 9.72) * mm, "mid": v(24.63, 9.64) * mm, "end": v(25.68, 9.38) * mm});
            skArc(sketch, "E13.19.6", {"start": v(25.99, 9.1) * mm, "mid": v(25.87, 9.27) * mm, "end": v(25.68, 9.38) * mm});
            skLineSegment(sketch, "E13.19.7", {"start": v(26.15, 8.6) * mm, "end": v(26.09, 8.86) * mm});
            skLineSegment(sketch, "E13.19.8", {"start": v(25.99, 9.1) * mm, "end": v(26.09, 8.86) * mm});
            skArc(sketch, "E13.19.9", {"start": v(26.09, 8.2) * mm, "mid": v(26.16, 8.4) * mm, "end": v(26.15, 8.6) * mm});
            skArc(sketch, "E13.19.10", {"start": v(24.46, 6.55) * mm, "mid": v(24.53, 6.58) * mm, "end": v(24.6, 6.62) * mm});
            skArc(sketch, "E13.19.11", {"start": v(23.55, 9.72) * mm, "mid": v(23.47, 9.71) * mm, "end": v(23.4, 9.7) * mm});
            skArc(sketch, "E13.20.0", {"start": v(18.1, 14.64) * mm, "mid": v(18.41, 14.46) * mm, "end": v(18.77, 14.54) * mm});
            skLineSegment(sketch, "E13.20.1", {"start": v(20.09, 15.42) * mm, "end": v(18.77, 14.54) * mm});
            skArc(sketch, "E13.20.2", {"start": v(20.62, 11.78) * mm, "mid": v(20.4, 11.48) * mm, "end": v(20.45, 11.11) * mm});
            skLineSegment(sketch, "E13.20.3", {"start": v(21.93, 12.66) * mm, "end": v(20.62, 11.78) * mm});
            skArc(sketch, "E13.20.4", {"start": v(22.05, 12.76) * mm, "mid": v(22.64, 13.67) * mm, "end": v(23.08, 14.66) * mm});
            skArc(sketch, "E13.20.5", {"start": v(20.23, 15.49) * mm, "mid": v(21.3, 15.69) * mm, "end": v(22.38, 15.7) * mm});
            skArc(sketch, "E13.20.6", {"start": v(22.75, 15.51) * mm, "mid": v(22.58, 15.65) * mm, "end": v(22.38, 15.7) * mm});
            skLineSegment(sketch, "E13.20.7", {"start": v(23.04, 15.08) * mm, "end": v(22.9, 15.3) * mm});
            skLineSegment(sketch, "E13.20.8", {"start": v(22.75, 15.51) * mm, "end": v(22.9, 15.3) * mm});
            skArc(sketch, "E13.20.9", {"start": v(23.08, 14.66) * mm, "mid": v(23.1, 14.88) * mm, "end": v(23.04, 15.08) * mm});
            skArc(sketch, "E13.20.10", {"start": v(21.93, 12.66) * mm, "mid": v(22, 12.7) * mm, "end": v(22.05, 12.76) * mm});
            skArc(sketch, "E13.20.11", {"start": v(20.23, 15.49) * mm, "mid": v(20.16, 15.46) * mm, "end": v(20.09, 15.42) * mm});
            skArc(sketch, "E13.21.0", {"start": v(13.69, 18.83) * mm, "mid": v(14.04, 18.73) * mm, "end": v(14.37, 18.9) * mm});
            skLineSegment(sketch, "E13.21.1", {"start": v(15.41, 20.1) * mm, "end": v(14.37, 18.9) * mm});
            skArc(sketch, "E13.21.2", {"start": v(16.87, 16.71) * mm, "mid": v(16.74, 16.37) * mm, "end": v(16.88, 16.03) * mm});
            skLineSegment(sketch, "E13.21.3", {"start": v(17.9, 17.9) * mm, "end": v(16.87, 16.71) * mm});
            skArc(sketch, "E13.21.4", {"start": v(18, 18.04) * mm, "mid": v(18.33, 19.06) * mm, "end": v(18.5, 20.14) * mm});
            skArc(sketch, "E13.21.5", {"start": v(15.53, 20.2) * mm, "mid": v(16.5, 20.67) * mm, "end": v(17.55, 20.97) * mm});
            skArc(sketch, "E13.21.6", {"start": v(17.96, 20.87) * mm, "mid": v(17.76, 20.96) * mm, "end": v(17.55, 20.97) * mm});
            skLineSegment(sketch, "E13.21.7", {"start": v(18.35, 20.53) * mm, "end": v(18.16, 20.71) * mm});
            skLineSegment(sketch, "E13.21.8", {"start": v(17.96, 20.87) * mm, "end": v(18.16, 20.71) * mm});
            skArc(sketch, "E13.21.9", {"start": v(18.5, 20.14) * mm, "mid": v(18.46, 20.35) * mm, "end": v(18.35, 20.53) * mm});
            skArc(sketch, "E13.21.10", {"start": v(17.9, 17.9) * mm, "mid": v(17.96, 17.97) * mm, "end": v(18, 18.04) * mm});
            skArc(sketch, "E13.21.11", {"start": v(15.53, 20.2) * mm, "mid": v(15.47, 20.15) * mm, "end": v(15.41, 20.1) * mm});
            skArc(sketch, "E13.22.0", {"start": v(8.35, 21.73) * mm, "mid": v(8.72, 21.73) * mm, "end": v(8.99, 21.98) * mm});
            skLineSegment(sketch, "E13.22.1", {"start": v(9.69, 23.4) * mm, "end": v(8.99, 21.98) * mm});
            skArc(sketch, "E13.22.2", {"start": v(11.97, 20.51) * mm, "mid": v(11.93, 20.14) * mm, "end": v(12.16, 19.85) * mm});
            skLineSegment(sketch, "E13.22.3", {"start": v(12.67, 21.93) * mm, "end": v(11.97, 20.51) * mm});
            skArc(sketch, "E13.22.4", {"start": v(12.71, 22.08) * mm, "mid": v(12.78, 23.16) * mm, "end": v(12.65, 24.24) * mm});
            skArc(sketch, "E13.22.5", {"start": v(9.78, 23.53) * mm, "mid": v(10.6, 24.23) * mm, "end": v(11.53, 24.8) * mm});
            skArc(sketch, "E13.22.6", {"start": v(11.94, 24.8) * mm, "mid": v(11.73, 24.85) * mm, "end": v(11.53, 24.8) * mm});
            skLineSegment(sketch, "E13.22.7", {"start": v(12.4, 24.58) * mm, "end": v(12.18, 24.7) * mm});
            skLineSegment(sketch, "E13.22.8", {"start": v(11.94, 24.8) * mm, "end": v(12.18, 24.7) * mm});
            skArc(sketch, "E13.22.9", {"start": v(12.65, 24.24) * mm, "mid": v(12.57, 24.43) * mm, "end": v(12.4, 24.58) * mm});
            skArc(sketch, "E13.22.10", {"start": v(12.67, 21.93) * mm, "mid": v(12.7, 22) * mm, "end": v(12.71, 22.08) * mm});
            skArc(sketch, "E13.22.11", {"start": v(9.78, 23.53) * mm, "mid": v(9.73, 23.46) * mm, "end": v(9.69, 23.4) * mm});
            skArc(sketch, "E13.23.0", {"start": v(2.44, 23.15) * mm, "mid": v(2.8, 23.25) * mm, "end": v(3, 23.56) * mm});
            skLineSegment(sketch, "E13.23.1", {"start": v(3.3, 25.1) * mm, "end": v(3, 23.56) * mm});
            skArc(sketch, "E13.23.2", {"start": v(6.25, 22.9) * mm, "mid": v(6.31, 22.55) * mm, "end": v(6.6, 22.32) * mm});
            skLineSegment(sketch, "E13.23.3", {"start": v(6.56, 24.46) * mm, "end": v(6.25, 22.9) * mm});
            skArc(sketch, "E13.23.4", {"start": v(6.56, 24.62) * mm, "mid": v(6.35, 25.68) * mm, "end": v(5.95, 26.69) * mm});
            skArc(sketch, "E13.23.5", {"start": v(3.36, 25.25) * mm, "mid": v(3.96, 26.15) * mm, "end": v(4.72, 26.93) * mm});
            skArc(sketch, "E13.23.6", {"start": v(5.12, 27.05) * mm, "mid": v(4.9, 27.04) * mm, "end": v(4.72, 26.93) * mm});
            skLineSegment(sketch, "E13.23.7", {"start": v(5.63, 26.95) * mm, "end": v(5.37, 27.02) * mm});
            skLineSegment(sketch, "E13.23.8", {"start": v(5.12, 27.05) * mm, "end": v(5.37, 27.02) * mm});
            skArc(sketch, "E13.23.9", {"start": v(5.95, 26.69) * mm, "mid": v(5.82, 26.85) * mm, "end": v(5.63, 26.95) * mm});
            skArc(sketch, "E13.23.10", {"start": v(6.56, 24.46) * mm, "mid": v(6.57, 24.54) * mm, "end": v(6.56, 24.62) * mm});
            skArc(sketch, "E13.23.11", {"start": v(3.36, 25.25) * mm, "mid": v(3.32, 25.18) * mm, "end": v(3.3, 25.1) * mm});
            skArc(sketch, "E14.trimOffspring", {"start": v(-9.46, 21.27) * mm, "mid": v(-10.3, 20.88) * mm, "end": v(-11.11, 20.45) * mm});
            skArc(sketch, "E15.trimOffspring", {"start": v(2.44, 23.15) * mm, "mid": v(1.52, 23.23) * mm, "end": v(0.6, 23.27) * mm});
            skArc(sketch, "E16.trimOffspring", {"start": v(8.35, 21.73) * mm, "mid": v(7.48, 22.04) * mm, "end": v(6.6, 22.32) * mm});
            skArc(sketch, "E17.trimOffspring", {"start": v(13.69, 18.83) * mm, "mid": v(12.93, 19.36) * mm, "end": v(12.16, 19.85) * mm});
            skArc(sketch, "E18.trimOffspring", {"start": v(18.1, 14.64) * mm, "mid": v(17.5, 15.35) * mm, "end": v(16.88, 16.03) * mm});
            skArc(sketch, "E19.trimOffspring", {"start": v(-14.64, 18.1) * mm, "mid": v(-15.35, 17.5) * mm, "end": v(-16.03, 16.88) * mm});
            skArc(sketch, "E20.trimOffspring", {"start": v(-18.83, 13.69) * mm, "mid": v(-19.36, 12.93) * mm, "end": v(-19.85, 12.16) * mm});
            skArc(sketch, "E21.trimOffspring", {"start": v(-21.73, 8.35) * mm, "mid": v(-22.04, 7.48) * mm, "end": v(-22.32, 6.6) * mm});
            skArc(sketch, "E22.trimOffspring", {"start": v(-23.15, 2.44) * mm, "mid": v(-23.23, 1.52) * mm, "end": v(-23.27, 0.6) * mm});
            skArc(sketch, "E23.trimOffspring", {"start": v(-23, -3.63) * mm, "mid": v(-22.83, -4.54) * mm, "end": v(-22.63, -5.44) * mm});
            skArc(sketch, "E24.trimOffspring", {"start": v(-21.27, -9.46) * mm, "mid": v(-20.88, -10.3) * mm, "end": v(-20.45, -11.11) * mm});
            skArc(sketch, "E25.trimOffspring", {"start": v(-18.1, -14.64) * mm, "mid": v(-17.5, -15.35) * mm, "end": v(-16.88, -16.03) * mm});
            skArc(sketch, "E26.trimOffspring", {"start": v(-13.69, -18.83) * mm, "mid": v(-12.93, -19.36) * mm, "end": v(-12.16, -19.85) * mm});
            skArc(sketch, "E27.trimOffspring", {"start": v(-8.35, -21.73) * mm, "mid": v(-7.48, -22.04) * mm, "end": v(-6.6, -22.32) * mm});
            skArc(sketch, "E28.trimOffspring", {"start": v(-2.44, -23.15) * mm, "mid": v(-1.52, -23.23) * mm, "end": v(-0.6, -23.27) * mm});
            skArc(sketch, "E29.trimOffspring", {"start": v(3.63, -23) * mm, "mid": v(4.54, -22.83) * mm, "end": v(5.44, -22.63) * mm});
            skArc(sketch, "E30.trimOffspring", {"start": v(9.46, -21.27) * mm, "mid": v(10.3, -20.88) * mm, "end": v(11.11, -20.45) * mm});
            skArc(sketch, "E31.trimOffspring", {"start": v(14.64, -18.1) * mm, "mid": v(15.35, -17.5) * mm, "end": v(16.03, -16.88) * mm});
            skArc(sketch, "E32.trimOffspring", {"start": v(18.83, -13.69) * mm, "mid": v(19.36, -12.93) * mm, "end": v(19.85, -12.16) * mm});
            skArc(sketch, "E33.trimOffspring", {"start": v(21.73, -8.35) * mm, "mid": v(22.04, -7.48) * mm, "end": v(22.32, -6.6) * mm});
            skArc(sketch, "E34.trimOffspring", {"start": v(23.15, -2.44) * mm, "mid": v(23.23, -1.52) * mm, "end": v(23.27, -0.6) * mm});
            skArc(sketch, "E35.trimOffspring", {"start": v(23, 3.63) * mm, "mid": v(22.83, 4.54) * mm, "end": v(22.63, 5.44) * mm});
            skArc(sketch, "E36.trimOffspring", {"start": v(21.27, 9.46) * mm, "mid": v(20.88, 10.3) * mm, "end": v(20.45, 11.11) * mm});
            skSolve(sketch);
        }
        {
            var Q0;
            Q0 = qSketchRegion(id + "F0", true);
            var Q1;
            Q1=makeQuery(id+"F0.imprint","IMPRINT",FACE,{"disambiguationData":[TD([[makeQuery(id+"F0.imprint","IMPRINT",EDGE,{"derivedFrom":sQuery(id+"F0.wireOp",EDGE,"E0")}),1.0]])]});
            extrude(context, id + "F1", {"entities" : qUnion([Q0, Q1]), "depth" : 12.7 * mm});
        }
        {
            var Q0;
            Q0=makeQuery(id+"F1.opExtrude","CAP_FACE",FACE,{"disambiguationData":[OSD([sQuery(id+"F0.wireOp",EDGE,"E0"),sQuery(id+"F0.wireOp",EDGE,"E1"),sQuery(id+"F0.wireOp",EDGE,"E2"),sQuery(id+"F0.wireOp",EDGE,"E3"),sQuery(id+"F0.wireOp",EDGE,"E4.MirrorCS"),sQuery(id+"F0.wireOp",EDGE,"E5.MirrorCS"),sQuery(id+"F0.wireOp",EDGE,"E6.MirrorCS"),sQuery(id+"F0.wireOp",EDGE,"E7.filletArc"),sQuery(id+"F0.wireOp",EDGE,"E8.filletArc"),sQuery(id+"F0.wireOp",EDGE,"E9.filletArc"),sQuery(id+"F0.wireOp",EDGE,"E10.filletArc"),sQuery(id+"F0.wireOp",EDGE,"E11.filletArc"),sQuery(id+"F0.wireOp",EDGE,"E12.filletArc"),sQuery(id+"F0.wireOp",EDGE,"E13.1.0"),sQuery(id+"F0.wireOp",EDGE,"E13.1.1"),sQuery(id+"F0.wireOp",EDGE,"E13.1.2"),sQuery(id+"F0.wireOp",EDGE,"E13.1.3"),sQuery(id+"F0.wireOp",EDGE,"E13.1.4"),sQuery(id+"F0.wireOp",EDGE,"E13.1.5"),sQuery(id+"F0.wireOp",EDGE,"E13.1.6"),sQuery(id+"F0.wireOp",EDGE,"E13.1.7"),sQuery(id+"F0.wireOp",EDGE,"E13.1.8"),sQuery(id+"F0.wireOp",EDGE,"E13.1.9"),sQuery(id+"F0.wireOp",EDGE,"E13.1.10"),sQuery(id+"F0.wireOp",EDGE,"E13.1.11"),sQuery(id+"F0.wireOp",EDGE,"E13.2.0"),sQuery(id+"F0.wireOp",EDGE,"E13.2.1"),sQuery(id+"F0.wireOp",EDGE,"E13.2.2"),sQuery(id+"F0.wireOp",EDGE,"E13.2.3"),sQuery(id+"F0.wireOp",EDGE,"E13.2.4"),sQuery(id+"F0.wireOp",EDGE,"E13.2.5"),sQuery(id+"F0.wireOp",EDGE,"E13.2.6"),sQuery(id+"F0.wireOp",EDGE,"E13.2.7"),sQuery(id+"F0.wireOp",EDGE,"E13.2.8"),sQuery(id+"F0.wireOp",EDGE,"E13.2.9"),sQuery(id+"F0.wireOp",EDGE,"E13.2.10"),sQuery(id+"F0.wireOp",EDGE,"E13.2.11"),sQuery(id+"F0.wireOp",EDGE,"E13.3.0"),sQuery(id+"F0.wireOp",EDGE,"E13.3.1"),sQuery(id+"F0.wireOp",EDGE,"E13.3.2"),sQuery(id+"F0.wireOp",EDGE,"E13.3.3"),sQuery(id+"F0.wireOp",EDGE,"E13.3.4"),sQuery(id+"F0.wireOp",EDGE,"E13.3.5"),sQuery(id+"F0.wireOp",EDGE,"E13.3.6"),sQuery(id+"F0.wireOp",EDGE,"E13.3.7"),sQuery(id+"F0.wireOp",EDGE,"E13.3.8"),sQuery(id+"F0.wireOp",EDGE,"E13.3.9"),sQuery(id+"F0.wireOp",EDGE,"E13.3.10"),sQuery(id+"F0.wireOp",EDGE,"E13.3.11"),sQuery(id+"F0.wireOp",EDGE,"E13.4.0"),sQuery(id+"F0.wireOp",EDGE,"E13.4.1"),sQuery(id+"F0.wireOp",EDGE,"E13.4.2"),sQuery(id+"F0.wireOp",EDGE,"E13.4.3"),sQuery(id+"F0.wireOp",EDGE,"E13.4.4"),sQuery(id+"F0.wireOp",EDGE,"E13.4.5"),sQuery(id+"F0.wireOp",EDGE,"E13.4.6"),sQuery(id+"F0.wireOp",EDGE,"E13.4.7"),sQuery(id+"F0.wireOp",EDGE,"E13.4.8"),sQuery(id+"F0.wireOp",EDGE,"E13.4.9"),sQuery(id+"F0.wireOp",EDGE,"E13.4.10"),sQuery(id+"F0.wireOp",EDGE,"E13.4.11"),sQuery(id+"F0.wireOp",EDGE,"E13.5.0"),sQuery(id+"F0.wireOp",EDGE,"E13.5.1"),sQuery(id+"F0.wireOp",EDGE,"E13.5.2"),sQuery(id+"F0.wireOp",EDGE,"E13.5.3"),sQuery(id+"F0.wireOp",EDGE,"E13.5.4"),sQuery(id+"F0.wireOp",EDGE,"E13.5.5"),sQuery(id+"F0.wireOp",EDGE,"E13.5.6"),sQuery(id+"F0.wireOp",EDGE,"E13.5.7"),sQuery(id+"F0.wireOp",EDGE,"E13.5.8"),sQuery(id+"F0.wireOp",EDGE,"E13.5.9"),sQuery(id+"F0.wireOp",EDGE,"E13.5.10"),sQuery(id+"F0.wireOp",EDGE,"E13.5.11"),sQuery(id+"F0.wireOp",EDGE,"E13.6.0"),sQuery(id+"F0.wireOp",EDGE,"E13.6.1"),sQuery(id+"F0.wireOp",EDGE,"E13.6.2"),sQuery(id+"F0.wireOp",EDGE,"E13.6.3"),sQuery(id+"F0.wireOp",EDGE,"E13.6.4"),sQuery(id+"F0.wireOp",EDGE,"E13.6.5"),sQuery(id+"F0.wireOp",EDGE,"E13.6.6"),sQuery(id+"F0.wireOp",EDGE,"E13.6.7"),sQuery(id+"F0.wireOp",EDGE,"E13.6.8"),sQuery(id+"F0.wireOp",EDGE,"E13.6.9"),sQuery(id+"F0.wireOp",EDGE,"E13.6.10"),sQuery(id+"F0.wireOp",EDGE,"E13.6.11"),sQuery(id+"F0.wireOp",EDGE,"E13.7.0"),sQuery(id+"F0.wireOp",EDGE,"E13.7.1"),sQuery(id+"F0.wireOp",EDGE,"E13.7.2"),sQuery(id+"F0.wireOp",EDGE,"E13.7.3"),sQuery(id+"F0.wireOp",EDGE,"E13.7.4"),sQuery(id+"F0.wireOp",EDGE,"E13.7.5"),sQuery(id+"F0.wireOp",EDGE,"E13.7.6"),sQuery(id+"F0.wireOp",EDGE,"E13.7.7"),sQuery(id+"F0.wireOp",EDGE,"E13.7.8"),sQuery(id+"F0.wireOp",EDGE,"E13.7.9"),sQuery(id+"F0.wireOp",EDGE,"E13.7.10"),sQuery(id+"F0.wireOp",EDGE,"E13.7.11"),sQuery(id+"F0.wireOp",EDGE,"E13.8.0"),sQuery(id+"F0.wireOp",EDGE,"E13.8.1"),sQuery(id+"F0.wireOp",EDGE,"E13.8.2"),sQuery(id+"F0.wireOp",EDGE,"E13.8.3"),sQuery(id+"F0.wireOp",EDGE,"E13.8.4"),sQuery(id+"F0.wireOp",EDGE,"E13.8.5"),sQuery(id+"F0.wireOp",EDGE,"E13.8.6"),sQuery(id+"F0.wireOp",EDGE,"E13.8.7"),sQuery(id+"F0.wireOp",EDGE,"E13.8.8"),sQuery(id+"F0.wireOp",EDGE,"E13.8.9"),sQuery(id+"F0.wireOp",EDGE,"E13.8.10"),sQuery(id+"F0.wireOp",EDGE,"E13.8.11"),sQuery(id+"F0.wireOp",EDGE,"E13.9.0"),sQuery(id+"F0.wireOp",EDGE,"E13.9.1"),sQuery(id+"F0.wireOp",EDGE,"E13.9.2"),sQuery(id+"F0.wireOp",EDGE,"E13.9.3"),sQuery(id+"F0.wireOp",EDGE,"E13.9.4"),sQuery(id+"F0.wireOp",EDGE,"E13.9.5"),sQuery(id+"F0.wireOp",EDGE,"E13.9.6"),sQuery(id+"F0.wireOp",EDGE,"E13.9.7"),sQuery(id+"F0.wireOp",EDGE,"E13.9.8"),sQuery(id+"F0.wireOp",EDGE,"E13.9.9"),sQuery(id+"F0.wireOp",EDGE,"E13.9.10"),sQuery(id+"F0.wireOp",EDGE,"E13.9.11"),sQuery(id+"F0.wireOp",EDGE,"E13.10.0"),sQuery(id+"F0.wireOp",EDGE,"E13.10.1"),sQuery(id+"F0.wireOp",EDGE,"E13.10.2"),sQuery(id+"F0.wireOp",EDGE,"E13.10.3"),sQuery(id+"F0.wireOp",EDGE,"E13.10.4"),sQuery(id+"F0.wireOp",EDGE,"E13.10.5"),sQuery(id+"F0.wireOp",EDGE,"E13.10.6"),sQuery(id+"F0.wireOp",EDGE,"E13.10.7"),sQuery(id+"F0.wireOp",EDGE,"E13.10.8"),sQuery(id+"F0.wireOp",EDGE,"E13.10.9"),sQuery(id+"F0.wireOp",EDGE,"E13.10.10"),sQuery(id+"F0.wireOp",EDGE,"E13.10.11"),sQuery(id+"F0.wireOp",EDGE,"E13.11.0"),sQuery(id+"F0.wireOp",EDGE,"E13.11.1"),sQuery(id+"F0.wireOp",EDGE,"E13.11.2"),sQuery(id+"F0.wireOp",EDGE,"E13.11.3"),sQuery(id+"F0.wireOp",EDGE,"E13.11.4"),sQuery(id+"F0.wireOp",EDGE,"E13.11.5"),sQuery(id+"F0.wireOp",EDGE,"E13.11.6"),sQuery(id+"F0.wireOp",EDGE,"E13.11.7"),sQuery(id+"F0.wireOp",EDGE,"E13.11.8"),sQuery(id+"F0.wireOp",EDGE,"E13.11.9"),sQuery(id+"F0.wireOp",EDGE,"E13.11.10"),sQuery(id+"F0.wireOp",EDGE,"E13.11.11"),sQuery(id+"F0.wireOp",EDGE,"E13.12.0"),sQuery(id+"F0.wireOp",EDGE,"E13.12.1"),sQuery(id+"F0.wireOp",EDGE,"E13.12.2"),sQuery(id+"F0.wireOp",EDGE,"E13.12.3"),sQuery(id+"F0.wireOp",EDGE,"E13.12.4"),sQuery(id+"F0.wireOp",EDGE,"E13.12.5"),sQuery(id+"F0.wireOp",EDGE,"E13.12.6"),sQuery(id+"F0.wireOp",EDGE,"E13.12.7"),sQuery(id+"F0.wireOp",EDGE,"E13.12.8"),sQuery(id+"F0.wireOp",EDGE,"E13.12.9"),sQuery(id+"F0.wireOp",EDGE,"E13.12.10"),sQuery(id+"F0.wireOp",EDGE,"E13.12.11"),sQuery(id+"F0.wireOp",EDGE,"E13.13.0"),sQuery(id+"F0.wireOp",EDGE,"E13.13.1"),sQuery(id+"F0.wireOp",EDGE,"E13.13.2"),sQuery(id+"F0.wireOp",EDGE,"E13.13.3"),sQuery(id+"F0.wireOp",EDGE,"E13.13.4"),sQuery(id+"F0.wireOp",EDGE,"E13.13.5"),sQuery(id+"F0.wireOp",EDGE,"E13.13.6"),sQuery(id+"F0.wireOp",EDGE,"E13.13.7"),sQuery(id+"F0.wireOp",EDGE,"E13.13.8"),sQuery(id+"F0.wireOp",EDGE,"E13.13.9"),sQuery(id+"F0.wireOp",EDGE,"E13.13.10"),sQuery(id+"F0.wireOp",EDGE,"E13.13.11"),sQuery(id+"F0.wireOp",EDGE,"E13.14.0"),sQuery(id+"F0.wireOp",EDGE,"E13.14.1"),sQuery(id+"F0.wireOp",EDGE,"E13.14.2"),sQuery(id+"F0.wireOp",EDGE,"E13.14.3"),sQuery(id+"F0.wireOp",EDGE,"E13.14.4"),sQuery(id+"F0.wireOp",EDGE,"E13.14.5"),sQuery(id+"F0.wireOp",EDGE,"E13.14.6"),sQuery(id+"F0.wireOp",EDGE,"E13.14.7"),sQuery(id+"F0.wireOp",EDGE,"E13.14.8"),sQuery(id+"F0.wireOp",EDGE,"E13.14.9"),sQuery(id+"F0.wireOp",EDGE,"E13.14.10"),sQuery(id+"F0.wireOp",EDGE,"E13.14.11"),sQuery(id+"F0.wireOp",EDGE,"E13.15.0"),sQuery(id+"F0.wireOp",EDGE,"E13.15.1"),sQuery(id+"F0.wireOp",EDGE,"E13.15.2"),sQuery(id+"F0.wireOp",EDGE,"E13.15.3"),sQuery(id+"F0.wireOp",EDGE,"E13.15.4"),sQuery(id+"F0.wireOp",EDGE,"E13.15.5"),sQuery(id+"F0.wireOp",EDGE,"E13.15.6"),sQuery(id+"F0.wireOp",EDGE,"E13.15.7"),sQuery(id+"F0.wireOp",EDGE,"E13.15.8"),sQuery(id+"F0.wireOp",EDGE,"E13.15.9"),sQuery(id+"F0.wireOp",EDGE,"E13.15.10"),sQuery(id+"F0.wireOp",EDGE,"E13.15.11"),sQuery(id+"F0.wireOp",EDGE,"E13.16.0"),sQuery(id+"F0.wireOp",EDGE,"E13.16.1"),sQuery(id+"F0.wireOp",EDGE,"E13.16.2"),sQuery(id+"F0.wireOp",EDGE,"E13.16.3"),sQuery(id+"F0.wireOp",EDGE,"E13.16.4"),sQuery(id+"F0.wireOp",EDGE,"E13.16.5"),sQuery(id+"F0.wireOp",EDGE,"E13.16.6"),sQuery(id+"F0.wireOp",EDGE,"E13.16.7"),sQuery(id+"F0.wireOp",EDGE,"E13.16.8"),sQuery(id+"F0.wireOp",EDGE,"E13.16.9"),sQuery(id+"F0.wireOp",EDGE,"E13.16.10"),sQuery(id+"F0.wireOp",EDGE,"E13.16.11"),sQuery(id+"F0.wireOp",EDGE,"E13.17.0"),sQuery(id+"F0.wireOp",EDGE,"E13.17.1"),sQuery(id+"F0.wireOp",EDGE,"E13.17.2"),sQuery(id+"F0.wireOp",EDGE,"E13.17.3"),sQuery(id+"F0.wireOp",EDGE,"E13.17.4"),sQuery(id+"F0.wireOp",EDGE,"E13.17.5"),sQuery(id+"F0.wireOp",EDGE,"E13.17.6"),sQuery(id+"F0.wireOp",EDGE,"E13.17.7"),sQuery(id+"F0.wireOp",EDGE,"E13.17.8"),sQuery(id+"F0.wireOp",EDGE,"E13.17.9"),sQuery(id+"F0.wireOp",EDGE,"E13.17.10"),sQuery(id+"F0.wireOp",EDGE,"E13.17.11"),sQuery(id+"F0.wireOp",EDGE,"E13.18.0"),sQuery(id+"F0.wireOp",EDGE,"E13.18.1"),sQuery(id+"F0.wireOp",EDGE,"E13.18.2"),sQuery(id+"F0.wireOp",EDGE,"E13.18.3"),sQuery(id+"F0.wireOp",EDGE,"E13.18.4"),sQuery(id+"F0.wireOp",EDGE,"E13.18.5"),sQuery(id+"F0.wireOp",EDGE,"E13.18.6"),sQuery(id+"F0.wireOp",EDGE,"E13.18.7"),sQuery(id+"F0.wireOp",EDGE,"E13.18.8"),sQuery(id+"F0.wireOp",EDGE,"E13.18.9"),sQuery(id+"F0.wireOp",EDGE,"E13.18.10"),sQuery(id+"F0.wireOp",EDGE,"E13.18.11"),sQuery(id+"F0.wireOp",EDGE,"E13.19.0"),sQuery(id+"F0.wireOp",EDGE,"E13.19.1"),sQuery(id+"F0.wireOp",EDGE,"E13.19.2"),sQuery(id+"F0.wireOp",EDGE,"E13.19.3"),sQuery(id+"F0.wireOp",EDGE,"E13.19.4"),sQuery(id+"F0.wireOp",EDGE,"E13.19.5"),sQuery(id+"F0.wireOp",EDGE,"E13.19.6"),sQuery(id+"F0.wireOp",EDGE,"E13.19.7"),sQuery(id+"F0.wireOp",EDGE,"E13.19.8"),sQuery(id+"F0.wireOp",EDGE,"E13.19.9"),sQuery(id+"F0.wireOp",EDGE,"E13.19.10"),sQuery(id+"F0.wireOp",EDGE,"E13.19.11"),sQuery(id+"F0.wireOp",EDGE,"E13.20.0"),sQuery(id+"F0.wireOp",EDGE,"E13.20.1"),sQuery(id+"F0.wireOp",EDGE,"E13.20.2"),sQuery(id+"F0.wireOp",EDGE,"E13.20.3"),sQuery(id+"F0.wireOp",EDGE,"E13.20.4"),sQuery(id+"F0.wireOp",EDGE,"E13.20.5"),sQuery(id+"F0.wireOp",EDGE,"E13.20.6"),sQuery(id+"F0.wireOp",EDGE,"E13.20.7"),sQuery(id+"F0.wireOp",EDGE,"E13.20.8"),sQuery(id+"F0.wireOp",EDGE,"E13.20.9"),sQuery(id+"F0.wireOp",EDGE,"E13.20.10"),sQuery(id+"F0.wireOp",EDGE,"E13.20.11"),sQuery(id+"F0.wireOp",EDGE,"E13.21.0"),sQuery(id+"F0.wireOp",EDGE,"E13.21.1"),sQuery(id+"F0.wireOp",EDGE,"E13.21.2"),sQuery(id+"F0.wireOp",EDGE,"E13.21.3"),sQuery(id+"F0.wireOp",EDGE,"E13.21.4"),sQuery(id+"F0.wireOp",EDGE,"E13.21.5"),sQuery(id+"F0.wireOp",EDGE,"E13.21.6"),sQuery(id+"F0.wireOp",EDGE,"E13.21.7"),sQuery(id+"F0.wireOp",EDGE,"E13.21.8"),sQuery(id+"F0.wireOp",EDGE,"E13.21.9"),sQuery(id+"F0.wireOp",EDGE,"E13.21.10"),sQuery(id+"F0.wireOp",EDGE,"E13.21.11"),sQuery(id+"F0.wireOp",EDGE,"E13.22.0"),sQuery(id+"F0.wireOp",EDGE,"E13.22.1"),sQuery(id+"F0.wireOp",EDGE,"E13.22.2"),sQuery(id+"F0.wireOp",EDGE,"E13.22.3"),sQuery(id+"F0.wireOp",EDGE,"E13.22.4"),sQuery(id+"F0.wireOp",EDGE,"E13.22.5"),sQuery(id+"F0.wireOp",EDGE,"E13.22.6"),sQuery(id+"F0.wireOp",EDGE,"E13.22.7"),sQuery(id+"F0.wireOp",EDGE,"E13.22.8"),sQuery(id+"F0.wireOp",EDGE,"E13.22.9"),sQuery(id+"F0.wireOp",EDGE,"E13.22.10"),sQuery(id+"F0.wireOp",EDGE,"E13.22.11"),sQuery(id+"F0.wireOp",EDGE,"E13.23.0"),sQuery(id+"F0.wireOp",EDGE,"E13.23.1"),sQuery(id+"F0.wireOp",EDGE,"E13.23.2"),sQuery(id+"F0.wireOp",EDGE,"E13.23.3"),sQuery(id+"F0.wireOp",EDGE,"E13.23.4"),sQuery(id+"F0.wireOp",EDGE,"E13.23.5"),sQuery(id+"F0.wireOp",EDGE,"E13.23.6"),sQuery(id+"F0.wireOp",EDGE,"E13.23.7"),sQuery(id+"F0.wireOp",EDGE,"E13.23.8"),sQuery(id+"F0.wireOp",EDGE,"E13.23.9"),sQuery(id+"F0.wireOp",EDGE,"E13.23.10"),sQuery(id+"F0.wireOp",EDGE,"E13.23.11"),sQuery(id+"F0.wireOp",EDGE,"E14.trimOffspring"),sQuery(id+"F0.wireOp",EDGE,"E15.trimOffspring"),sQuery(id+"F0.wireOp",EDGE,"E16.trimOffspring"),sQuery(id+"F0.wireOp",EDGE,"E17.trimOffspring"),sQuery(id+"F0.wireOp",EDGE,"E18.trimOffspring"),sQuery(id+"F0.wireOp",EDGE,"E19.trimOffspring"),sQuery(id+"F0.wireOp",EDGE,"E20.trimOffspring"),sQuery(id+"F0.wireOp",EDGE,"E21.trimOffspring"),sQuery(id+"F0.wireOp",EDGE,"E22.trimOffspring"),sQuery(id+"F0.wireOp",EDGE,"E23.trimOffspring"),sQuery(id+"F0.wireOp",EDGE,"E24.trimOffspring"),sQuery(id+"F0.wireOp",EDGE,"E25.trimOffspring"),sQuery(id+"F0.wireOp",EDGE,"E26.trimOffspring"),sQuery(id+"F0.wireOp",EDGE,"E27.trimOffspring"),sQuery(id+"F0.wireOp",EDGE,"E28.trimOffspring"),sQuery(id+"F0.wireOp",EDGE,"E29.trimOffspring"),sQuery(id+"F0.wireOp",EDGE,"E30.trimOffspring"),sQuery(id+"F0.wireOp",EDGE,"E31.trimOffspring"),sQuery(id+"F0.wireOp",EDGE,"E32.trimOffspring"),sQuery(id+"F0.wireOp",EDGE,"E33.trimOffspring"),sQuery(id+"F0.wireOp",EDGE,"E34.trimOffspring"),sQuery(id+"F0.wireOp",EDGE,"E35.trimOffspring"),sQuery(id+"F0.wireOp",EDGE,"E36.trimOffspring")])],"isStart":false});
            var sketch = newSketch(context, id + "F2", { "sketchPlane" : qUnion([Q0])});
            skCircle(sketch, "E37", {"center": v(0, 0) * mm, "radius": 6.35 * mm});
            skSolve(sketch);
        }
        {
            var Q0;
            Q0 = qSketchRegion(id + "F2", true);
            extrude(context, id + "F3", {"entities" : qUnion([Q0]), "operationType" : NewBodyOperationType.REMOVE, "oppositeDirection" : true, "depth" : 6.35 * mm});
        }
    });
